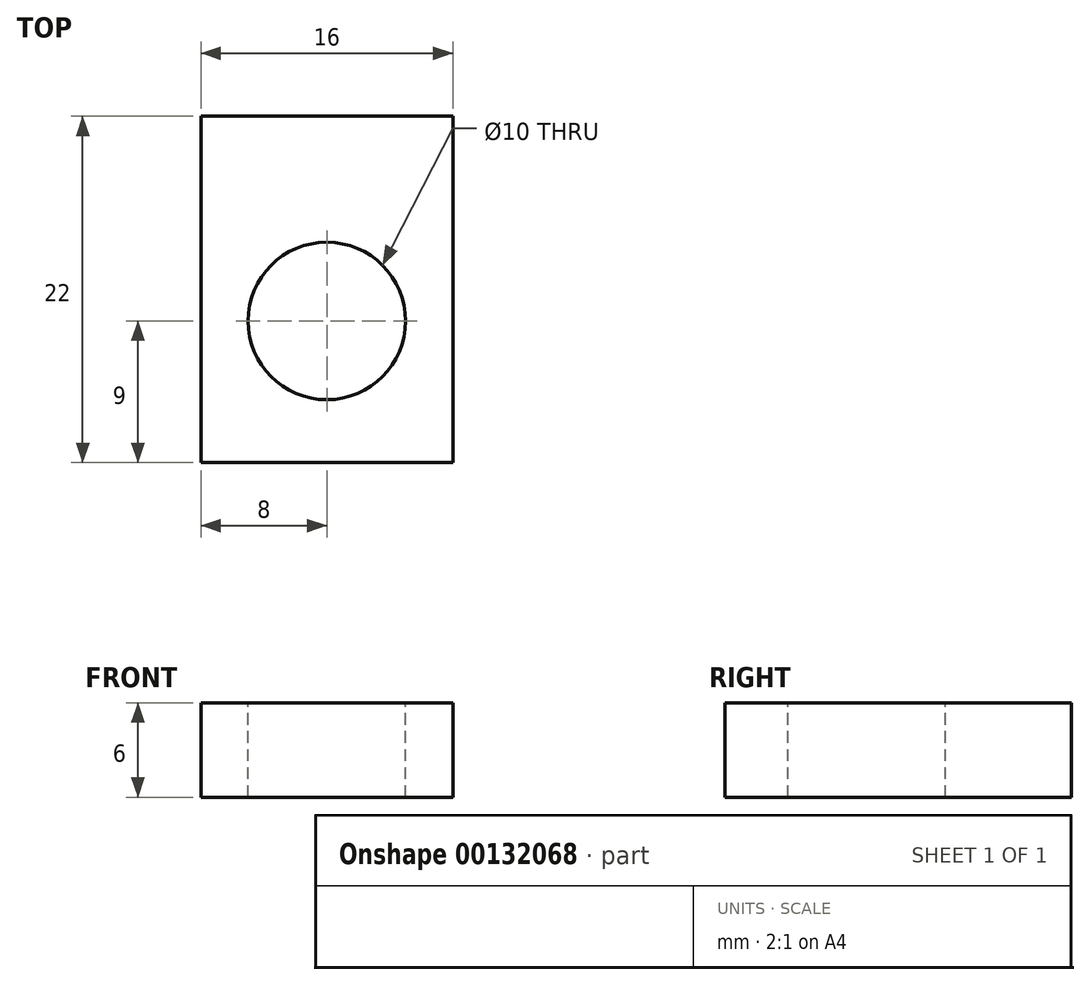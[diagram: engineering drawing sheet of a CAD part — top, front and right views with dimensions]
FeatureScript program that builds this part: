
annotation { "Feature Type Name" : "Feature", "Feature Type Description" : "" }
export const myFeature = defineFeature(function(context is Context, id is Id, definition is map)
    precondition{}
    {
        {
            var Q0;
            Q0=qCreatedBy(makeId("Top.planeOp"),FACE);
            var sketch = newSketch(context, id + "F0", { "sketchPlane" : qUnion([Q0])});
            skLineSegment(sketch, "E0.bottom", {"start": v(0, 0) * mm, "end": v(16, 0) * mm});
            skLineSegment(sketch, "E0.top", {"start": v(0, -22) * mm, "end": v(16, -22) * mm});
            skLineSegment(sketch, "E0.left", {"start": v(0, 0) * mm, "end": v(0, -22) * mm});
            skLineSegment(sketch, "E0.right", {"start": v(16, 0) * mm, "end": v(16, -22) * mm});
            skSolve(sketch);
        }
        {
            var Q0;
            Q0 = qSketchRegion(id + "F0", true);
            extrude(context, id + "F1", {"entities" : qUnion([Q0]), "depth" : 6 * mm});
        }
        {
            var Q0;
            Q0=makeQuery(id+"F1.opExtrude","CAP_FACE",FACE,{"disambiguationData":[OSD([sQuery(id+"F0.wireOp",EDGE,"E0.bottom"),sQuery(id+"F0.wireOp",EDGE,"E0.top"),sQuery(id+"F0.wireOp",EDGE,"E0.left"),sQuery(id+"F0.wireOp",EDGE,"E0.right")])],"isStart":false});
            var sketch = newSketch(context, id + "F2", { "sketchPlane" : qUnion([Q0])});
            skCircle(sketch, "E1", {"center": v(8, -13) * mm, "radius": 4.64 * mm});
            skSolve(sketch);
        }
        {
            var Q0;
            Q0=sQuery(id+"F2.wireOp",VERTEX,"E1.center");
            var Q1;
            Q1=makeQuery(id+"F1.opExtrude","SWEPT_BODY",BODY,{"disambiguationData":[OSD([sQuery(id+"F0.wireOp",EDGE,"E0.bottom"),sQuery(id+"F0.wireOp",EDGE,"E0.top"),sQuery(id+"F0.wireOp",EDGE,"E0.left"),sQuery(id+"F0.wireOp",EDGE,"E0.right")])]});
            hole(context, id + "F3", {"style" : HoleStyle.SIMPLE, "endStyle" : HoleEndStyle.THROUGH, "holeDiameter" : 10 * mm, "startFromSketch" : true, "locations" : qUnion([Q0]), "scope" : qUnion([Q1]), "isTappedThrough" : true});
        }
    });
